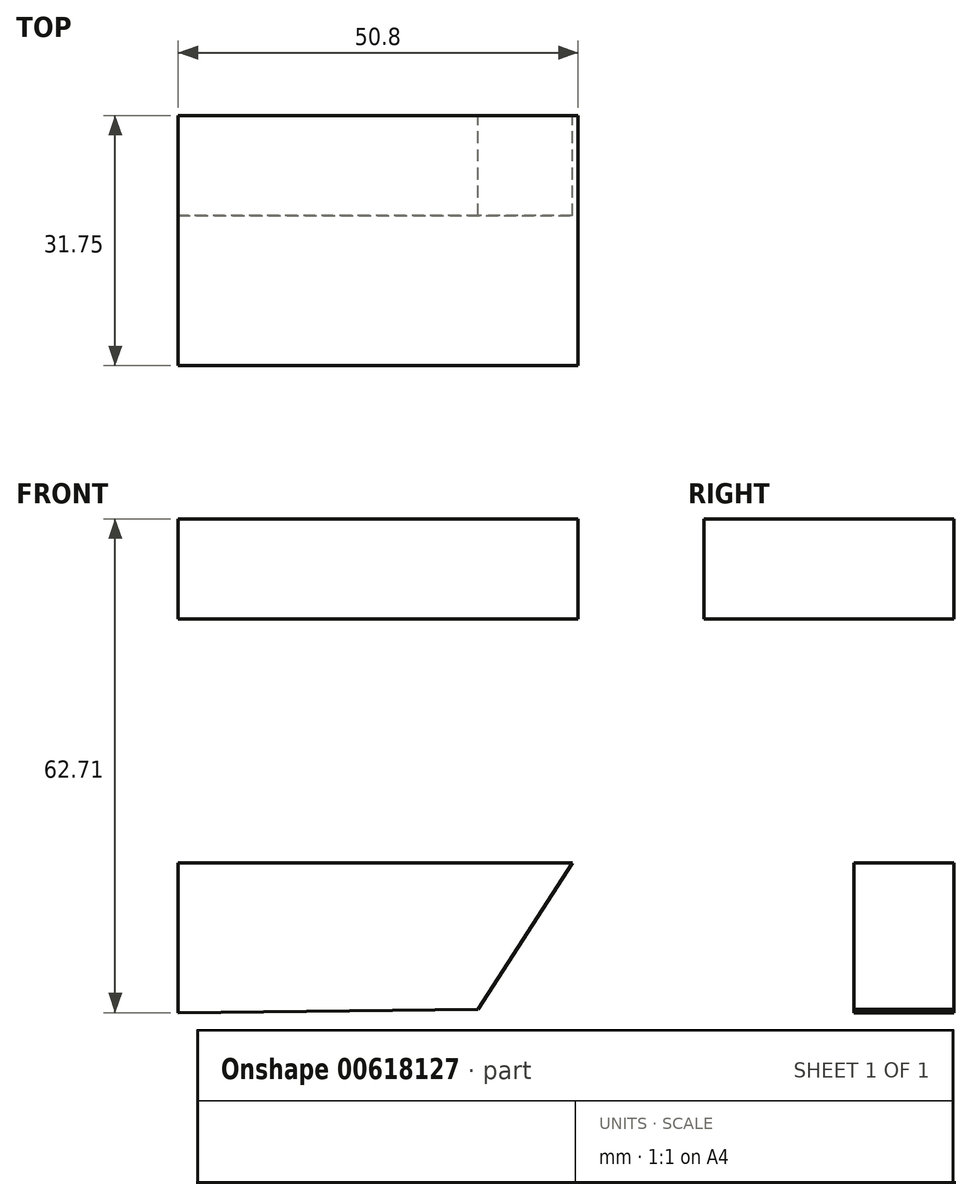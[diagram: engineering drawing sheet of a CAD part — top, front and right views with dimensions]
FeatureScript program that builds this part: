
annotation { "Feature Type Name" : "Feature", "Feature Type Description" : "" }
export const myFeature = defineFeature(function(context is Context, id is Id, definition is map)
    precondition{}
    {
        {
            var Q0;
            Q0=qCreatedBy(makeId("Top.planeOp"),FACE);
            var sketch = newSketch(context, id + "F0", { "sketchPlane" : qUnion([Q0])});
            skLineSegment(sketch, "E0", {"start": v(0, 0) * mm, "end": v(0, -31.75) * mm});
            skLineSegment(sketch, "E1", {"start": v(0, -31.75) * mm, "end": v(50.8, -31.75) * mm});
            skLineSegment(sketch, "E2", {"start": v(50.8, -31.75) * mm, "end": v(50.8, 0) * mm});
            skLineSegment(sketch, "E3", {"start": v(50.8, 0) * mm, "end": v(0, 0) * mm});
            skSolve(sketch);
        }
        {
            var Q0;
            Q0=makeQuery(id+"F0.imprint","IMPRINT",FACE,{"disambiguationData":[TD([[makeQuery(id+"F0.imprint","IMPRINT",EDGE,{"derivedFrom":sQuery(id+"F0.wireOp",EDGE,"E0")}),1.0]])]});
            extrude(context, id + "F1", {"entities" : qUnion([Q0]), "depth" : 12.7 * mm, "offsetDistance" : 25.4 * mm});
        }
        {
            var Q0;
            Q0=qCreatedBy(makeId("Front.planeOp"),FACE);
            var sketch = newSketch(context, id + "F2", { "sketchPlane" : qUnion([Q0])});
            skLineSegment(sketch, "E4", {"start": v(0, -50) * mm, "end": v(0, -30.96) * mm});
            skLineSegment(sketch, "E5", {"start": v(0, -30.96) * mm, "end": v(50.05, -30.96) * mm});
            skLineSegment(sketch, "E6", {"start": v(50.05, -30.96) * mm, "end": v(38.1, -49.6) * mm});
            skLineSegment(sketch, "E7", {"start": v(38.1, -49.6) * mm, "end": v(0, -50) * mm});
            skSolve(sketch);
        }
        {
            var Q0;
            Q0=makeQuery(id+"F2.imprint","IMPRINT",FACE,{"disambiguationData":[TD([[makeQuery(id+"F2.imprint","IMPRINT",EDGE,{"derivedFrom":sQuery(id+"F2.wireOp",EDGE,"E4")}),-1.0]])]});
            extrude(context, id + "F3", {"entities" : qUnion([Q0]), "depth" : 12.7 * mm, "offsetDistance" : 25.4 * mm});
        }
    });
